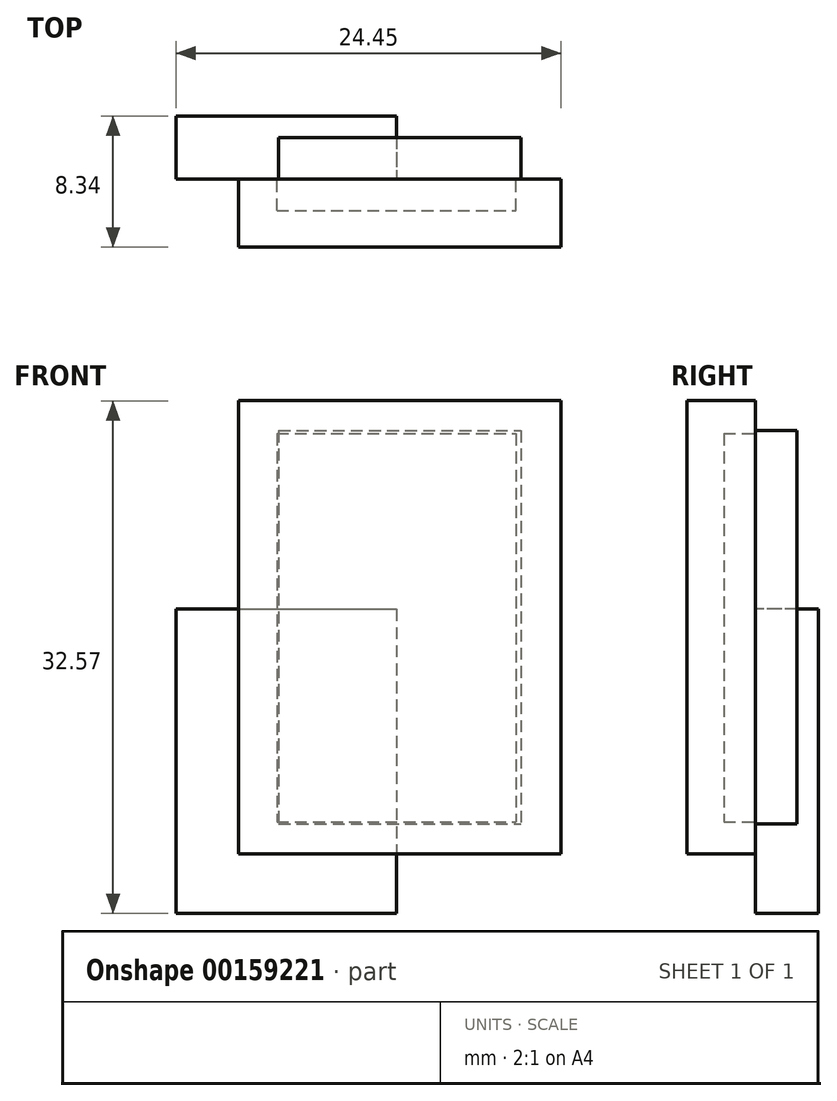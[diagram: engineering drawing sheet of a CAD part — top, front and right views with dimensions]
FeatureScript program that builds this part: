
annotation { "Feature Type Name" : "Feature", "Feature Type Description" : "" }
export const myFeature = defineFeature(function(context is Context, id is Id, definition is map)
    precondition{}
    {
        {
            var Q0;
            Q0=qCreatedBy(makeId("Front.planeOp"),FACE);
            var sketch = newSketch(context, id + "F0", { "sketchPlane" : qUnion([Q0])});
            skLineSegment(sketch, "E0.bottom", {"start": v(-52.52, 39.96) * mm, "end": v(-37.13, 39.96) * mm});
            skLineSegment(sketch, "E0.top", {"start": v(-52.52, 14.98) * mm, "end": v(-37.13, 14.98) * mm});
            skLineSegment(sketch, "E0.left", {"start": v(-52.52, 39.96) * mm, "end": v(-52.52, 14.98) * mm});
            skLineSegment(sketch, "E0.right", {"start": v(-37.13, 39.96) * mm, "end": v(-37.13, 14.98) * mm});
            skSolve(sketch);
        }
        {
            var Q0;
            Q0=qSketchRegion(id+"F0",true);
            extrude(context, id + "F1", {"entities" : qUnion([Q0]), "oppositeDirection" : true, "depth" : 2.64 * mm});
        }
        {
            var Q0;
            Q0=qCreatedBy(makeId("Front.planeOp"),FACE);
            var sketch = newSketch(context, id + "F2", { "sketchPlane" : qUnion([Q0])});
            skLineSegment(sketch, "E1.bottom", {"start": v(-55.07, 41.86) * mm, "end": v(-34.58, 41.86) * mm});
            skLineSegment(sketch, "E1.top", {"start": v(-55.07, 13.09) * mm, "end": v(-34.58, 13.09) * mm});
            skLineSegment(sketch, "E1.left", {"start": v(-55.07, 41.86) * mm, "end": v(-55.07, 13.09) * mm});
            skLineSegment(sketch, "E1.right", {"start": v(-34.58, 41.86) * mm, "end": v(-34.58, 13.09) * mm});
            skSolve(sketch);
        }
        {
            var Q0;
            Q0=qSketchRegion(id+"F2",true);
            extrude(context, id + "F3", {"entities" : qUnion([Q0]), "depth" : 4.34 * mm});
        }
        {
            var Q0;
            Q0=qCreatedBy(makeId("Front.planeOp"),FACE);
            var sketch = newSketch(context, id + "F4", { "sketchPlane" : qUnion([Q0])});
            skLineSegment(sketch, "E2.bottom", {"start": v(-52.63, 39.77) * mm, "end": v(-37.44, 39.77) * mm});
            skLineSegment(sketch, "E2.top", {"start": v(-52.63, 15.1) * mm, "end": v(-37.44, 15.1) * mm});
            skLineSegment(sketch, "E2.left", {"start": v(-52.63, 39.77) * mm, "end": v(-52.63, 15.1) * mm});
            skLineSegment(sketch, "E2.right", {"start": v(-37.44, 39.77) * mm, "end": v(-37.44, 15.1) * mm});
            skSolve(sketch);
        }
        {
            var Q0;
            Q0=qSketchRegion(id+"F4",true);
            extrude(context, id + "F5", {"entities" : qUnion([Q0]), "operationType" : NewBodyOperationType.REMOVE, "depth" : 2 * mm});
        }
        {
            var Q0;
            Q0=qCreatedBy(makeId("Front.planeOp"),FACE);
            var sketch = newSketch(context, id + "F6", { "sketchPlane" : qUnion([Q0])});
            skLineSegment(sketch, "E3.bottom", {"start": v(-59.03, 28.62) * mm, "end": v(-45.03, 28.62) * mm});
            skLineSegment(sketch, "E3.top", {"start": v(-59.03, 9.29) * mm, "end": v(-45.03, 9.29) * mm});
            skLineSegment(sketch, "E3.left", {"start": v(-59.03, 28.62) * mm, "end": v(-59.03, 9.29) * mm});
            skLineSegment(sketch, "E3.right", {"start": v(-45.03, 28.62) * mm, "end": v(-45.03, 9.29) * mm});
            skSolve(sketch);
        }
        {
            var Q0;
            Q0=qSketchRegion(id+"F6",true);
            extrude(context, id + "F7", {"entities" : qUnion([Q0]), "oppositeDirection" : true, "depth" : 4 * mm});
        }
    });
